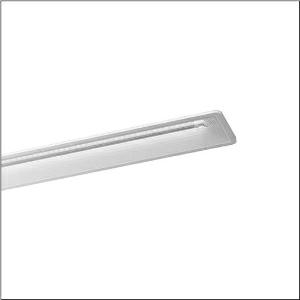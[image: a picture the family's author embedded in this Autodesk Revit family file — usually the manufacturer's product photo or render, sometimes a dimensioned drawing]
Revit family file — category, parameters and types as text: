
# Revit family: taris_r__21_5mt116d04wd_aa9a
name_source: partatom
category: Lighting Fixtures
units: mm (PartAtom-declared; Revit-internal decimal feet)

## family parameters
Cut with Voids When Loaded = No
Host = Face
Light Source = No
Part Type = Normal
Room Calculation Point = No
Round Connector Dimension = Use Diameter
Shared = No

## types (1)
- --- (1 x LED, 4910 lm, 28.9 W, 4000K)
    Apparent Load = 29 VA
    CIE Flux Codes = 73 96 99 100 100
    Color Rendering = 80
    Color Temperature = 4000K
    Default Elevation = 1800 mm
    Description = Taris® 21, office luminaire, primary anti-glare with micro louvre, primary optical cover: axial lens, of PMMA, structured, CAT 2 (L<= 1500cd/m²), light emission: direct distribution, primary light characteristic: symmetric, installation type: recessed, LED, rated luminous flux: 4.910lm, luminous efficacy: 170lm/W, light colour: 840, colour temperature: 4000K, control gear: ECG DALI, with terminal, 5-pole, mains connection: 230V, AC, 50Hz, rated input power: 29W, housing, luminaire housing, of plastic, traffic white (RAL 9016), module: M625, length: 1.250mm, width: 150mm, height: 76mm, recess depth: 106mm, protection rating (complete): IP20, insulation class (complete): insulation class I (protective earthing), certification: CE, ENEC, VDE, protection symbol: F, impact resistance: IK02, permissible operating ambient temperature: 0..+35°C, standard: EN 50419, packaging unit: 1 piece
    Height = 0 mm  [stored 0 ft]
    Lamp = 1 x LED
    Lamp Light Flux = 4910 lm
    Lamp Power = 28.9 W
    Lamp count = 1
    Length = 1243 mm
    Luminous efficacy = 170 lm/W
    Manufacturer = Siteco
    ModVariant = No
    Model = 5MT116D04WD
    Mounting Place = Ceiling
    Mounting Type = Recessed
    Number of Poles = 1
    OnlyDefault = Yes
    Power Factor = 1
    Product Name = Taris® 21
    Product group = office luminaire | ceiling recessed
    ProductGroupID = 401
    Protection Class = Protection class I
    Protection Degree = IP 20
    RLX_Detail_Level = 1
    RLX_Emergency_Light_Flux = 0 lm
    RLX_Emergency_Type = 0
    RLX_Emergency_Type_DB = No
    RlxData = <blob elided: 29993 chars, md5=2cba7822>
    Socket = socket
    Standby Power = 0 W
    System Light Flux = 4910 lm
    System Power = 29 W
    Type Comments = factory setting: luminous flux: 100 % | dim-lin: 254 | 200 mA
    Type Image = l_1004723.jpg
    URL = http://relux.com
    VarID = @adj_136847
    Voltage = 0 V
    Weight = 0.00 kg
    Width = 144 mm

note: [stored X ft] marks values corroborated as IEEE doubles in the binary element streams (Revit-internal decimal feet)

## geometry (parser evidence)
native form markers: Blend x4, Sweep x10
no freeform markers — native parametric forms only
